# Revit family: 6706
name_source: partatom
category: Plumbing Fixtures
units: mm (PartAtom-declared; Revit-internal decimal feet)

## family parameters
Cut with Voids When Loaded = No
Host = Face
OmniClass Number = 23.65.70.11.11
OmniClass Title = Fixtures for Liquids
Part Type = Normal
Room Calculation Point = No
Round Connector Dimension = Use Diameter
Shared = No

## types (2) — shared parameters
Gallons Per Minute = 0.000 GPM
Model number = L1
z Error = No
z GPM GPM = 0.000 GPM
z Has Rebuild Kit Trim Only = No
z Has Trim = No
zero-valued in all types: Default Elevation, z GPM Number, z Type GPM

## per-type parameters (varying)
| type | Date Modified | Description | Equipment Abbreviation | Family Version | Manufacturer | Model | Model Disclaimer | Product Documentation Link | Product Material | Product Page URL | Product data url | URL | z Type | z Type Finish |
| Chrome | January 30, 2015 | Shower System with Symmons Temptrol mixing valve, Chrome | TSS | 1.0 | Symmons Industries, Inc. | 3501-CYL-B | Contact Symmons Industries, Inc. For More Information | http://www.symmons.com | Chrome - Symmons - Polished | http://www.symmons.com | https://bimobject.com | http://www.symmons.com | 1 | 1 |
| Satin Nickel |  |  |  |  |  |  |  |  | Nickel - Symmons - Satin |  |  |  | 2 | 2 |

## geometry (parser evidence)
native form markers: Blend x4, Sweep x15
no freeform markers — native parametric forms only
